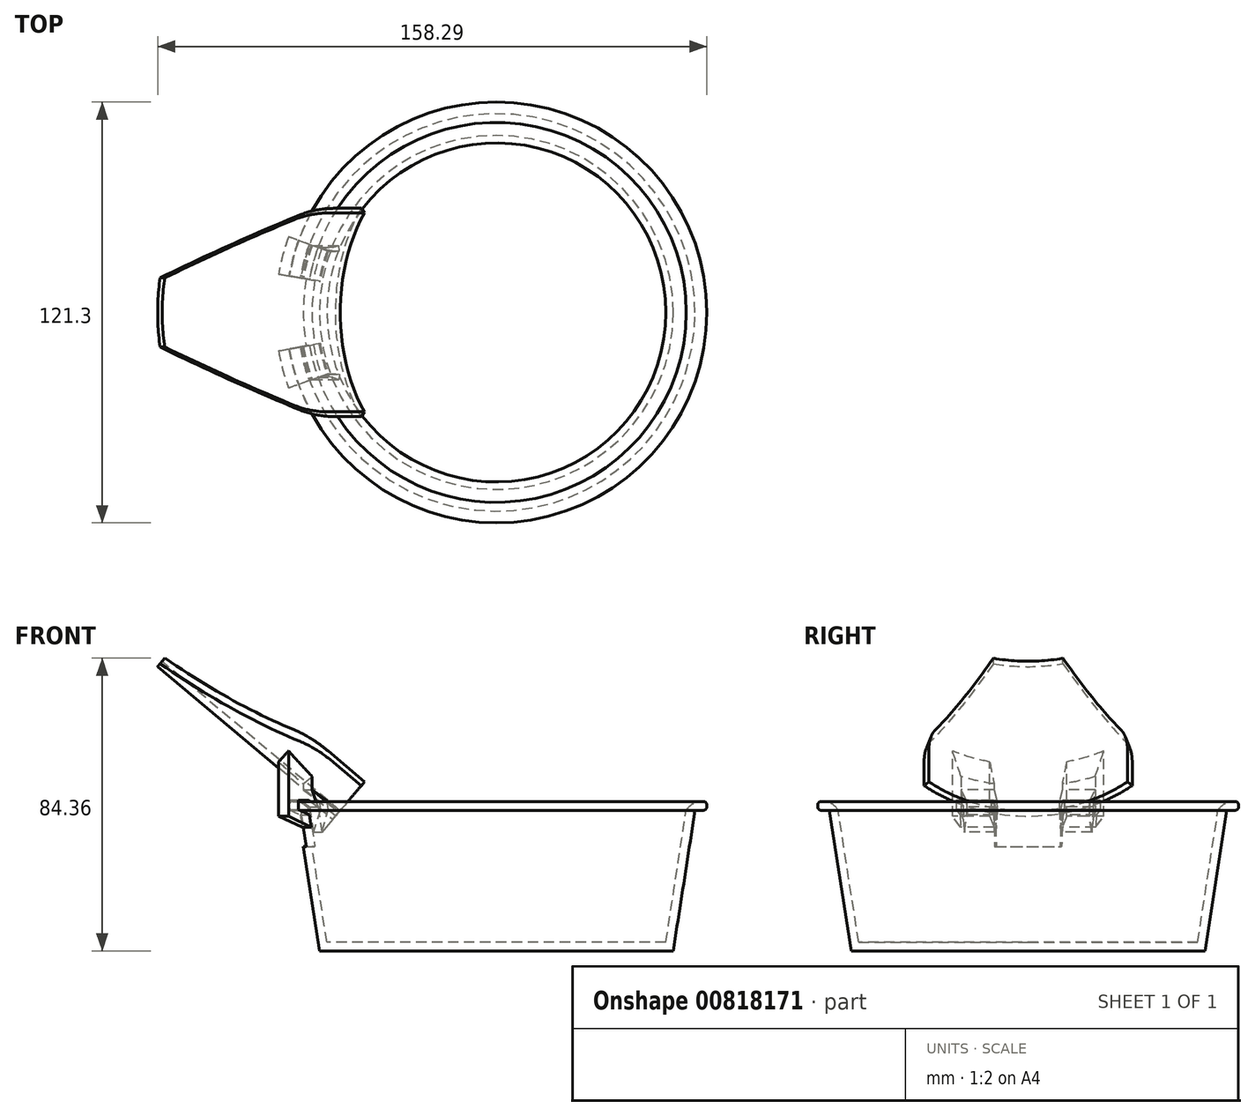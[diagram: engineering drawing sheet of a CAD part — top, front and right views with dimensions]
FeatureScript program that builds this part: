
annotation { "Feature Type Name" : "Feature", "Feature Type Description" : "" }
export const myFeature = defineFeature(function(context is Context, id is Id, definition is map)
    precondition{}
    {
        {
            var Q0;
            Q0=qCreatedBy(makeId("Front.planeOp"),FACE);
            var sketch = newSketch(context, id + "F0", { "sketchPlane" : qUnion([Q0])});
            skLineSegment(sketch, "E0", {"start": v(0, 0) * mm, "end": v(0, 46.12) * mm, "construction": true});
            skSolve(sketch);
        }
        {
            var Q0;
            Q0=qCreatedBy(makeId("Top.planeOp"),FACE);
            var sketch = newSketch(context, id + "F1", { "sketchPlane" : qUnion([Q0])});
            skCircle(sketch, "E1", {"center": v(0, 0) * mm, "radius": 51 * mm});
            skSolve(sketch);
        }
        {
            var Q0;
            Q0=qCreatedBy(makeId("Top.planeOp"),FACE);
            cPlane(context, id + "F2", {"entities" : qUnion([Q0]), "cplaneType" : CPlaneType.OFFSET, "offset" : 40.5 * mm, "width" : 150 * mm, "height" : 150 * mm});
        }
        {
            var Q0;
            Q0=qCreatedBy(id+"F2.planeOp",FACE);
            var sketch = newSketch(context, id + "F3", { "sketchPlane" : qUnion([Q0])});
            skCircle(sketch, "E2", {"center": v(0, 0) * mm, "radius": 57.27 * mm});
            skSolve(sketch);
        }
        {
            var Q0;
            Q0=makeQuery(id+"F1.imprint","IMPRINT",FACE,{"disambiguationData":[TD([[makeQuery(id+"F1.imprint","IMPRINT",EDGE,{"derivedFrom":sQuery(id+"F1.wireOp",EDGE,"E1")}),1.0]])]});
            var Q1;
            Q1=makeQuery(id+"F3.imprint","IMPRINT",FACE,{"disambiguationData":[TD([[makeQuery(id+"F3.imprint","IMPRINT",EDGE,{"derivedFrom":sQuery(id+"F3.wireOp",EDGE,"E2")}),1.0]])]});
            loft(context, id + "F4", {"sheetProfilesArray" : [{ "sheetProfileEntities" : qUnion([Q0]) }, { "sheetProfileEntities" : qUnion([Q1]) }]});
        }
        {
            var Q0;
            Q0=makeQuery(id+"F4.opLoft","CAP_FACE",FACE,{"disambiguationData":[OSD([makeQuery(id+"F3.imprint","IMPRINT",FACE,{"disambiguationData":[TD([[makeQuery(id+"F3.imprint","IMPRINT",EDGE,{"derivedFrom":sQuery(id+"F3.wireOp",EDGE,"E2")}),1.0]])]})])],"isStart":true});
            var sketch = newSketch(context, id + "F5", { "sketchPlane" : qUnion([Q0])});
            skCircle(sketch, "E3", {"center": v(0, 0) * mm, "radius": 60.65 * mm});
            skSolve(sketch);
        }
        {
            var Q0;
            Q0=makeQuery(id+"F4.opLoft","CAP_FACE",FACE,{"disambiguationData":[OSD([makeQuery(id+"F3.imprint","IMPRINT",FACE,{"disambiguationData":[TD([[makeQuery(id+"F3.imprint","IMPRINT",EDGE,{"derivedFrom":sQuery(id+"F3.wireOp",EDGE,"E2")}),1.0]])]})])],"isStart":true});
            shell(context, id + "F6", {"entities" : qUnion([Q0]), "thickness" : 2.5 * mm});
        }
        {
            var Q0;
            Q0=makeQuery(id+"F5.imprint","IMPRINT",FACE,{"disambiguationData":[TD([[makeQuery(id+"F5.imprint","IMPRINT",EDGE,{"derivedFrom":sQuery(id+"F5.wireOp",EDGE,"E3")}),1.0]])]});
            var Q1;
            Q1=makeQuery(id+"F4.opLoft","CAP_FACE",FACE,{"disambiguationData":[OSD([makeQuery(id+"F3.imprint","IMPRINT",FACE,{"disambiguationData":[TD([[makeQuery(id+"F3.imprint","IMPRINT",EDGE,{"derivedFrom":sQuery(id+"F3.wireOp",EDGE,"E2")}),1.0]])]})])],"isStart":true});
            extrude(context, id + "F7", {"entities" : qUnion([Q0, Q1]), "operationType" : NewBodyOperationType.ADD, "depth" : 2.55 * mm, "offsetDistance" : 25 * mm});
        }
        {
            var Q0;
            Q0=makeQuery(id+"F7.opExtrude","CAP_EDGE",EDGE,{"disambiguationData":[OSD([sQuery(id+"F5.wireOp",EDGE,"E3")])],"isStart":false});
            var Q1;
            Q1=makeQuery(id+"F7.opExtrude","CAP_EDGE",EDGE,{"disambiguationData":[OSD([sQuery(id+"F5.wireOp",EDGE,"E3")])],"isStart":true});
            fillet(context, id + "F8", {"entities" : qUnion([Q0, Q1]), "radius" : 1 * mm, "tangentPropagation" : true, "allowEdgeOverflow" : false});
        }
        {
            var Q0;
            {var subQ0=sQuery(id+"F3.wireOp",EDGE,"E2");Q0=makeQuery(id+"F7.opExtrude","CAP_EDGE",EDGE,{"disambiguationData":[OSD([subQ0]),TDD([makeQuery(id+"F6.opShell","OFFSET_EDGE",EDGE,{"disambiguationData":[OSD([subQ0])]})])],"isStart":false});}
            fillet(context, id + "F9", {"entities" : qUnion([Q0]), "radius" : 5 * mm, "tangentPropagation" : true, "allowEdgeOverflow" : false});
        }
        {
            var Q0;
            Q0=qCreatedBy(makeId("Front.planeOp"),FACE);
            var sketch = newSketch(context, id + "F10", { "sketchPlane" : qUnion([Q0])});
            skLineSegment(sketch, "E4", {"start": v(-57.38, 39.2) * mm, "end": v(-56.83, 35.67) * mm});
            skLineSegment(sketch, "E5", {"start": v(-56.83, 35.67) * mm, "end": v(-63.75, 38.75) * mm});
            skLineSegment(sketch, "E6", {"start": v(-63.75, 38.75) * mm, "end": v(-63.75, 46.4) * mm});
            skLineSegment(sketch, "E7", {"start": v(-63.75, 46.4) * mm, "end": v(-60.75, 46.4) * mm});
            skLineSegment(sketch, "E8", {"start": v(-60.75, 46.4) * mm, "end": v(-60.75, 40.7) * mm});
            skLineSegment(sketch, "E9", {"start": v(-60.75, 40.7) * mm, "end": v(-57.38, 39.2) * mm});
            skLineSegment(sketch, "E10", {"start": v(-60.75, 43.4) * mm, "end": v(-57.45, 43.4) * mm});
            skLineSegment(sketch, "E11", {"start": v(-57.45, 43.4) * mm, "end": v(-54.7, 41.5) * mm});
            skLineSegment(sketch, "E12", {"start": v(-54.7, 41.5) * mm, "end": v(-53.57, 34.22) * mm});
            skLineSegment(sketch, "E13", {"start": v(-53.57, 34.22) * mm, "end": v(-51.55, 40.76) * mm});
            skLineSegment(sketch, "E14", {"start": v(-51.55, 40.76) * mm, "end": v(-51.93, 43.23) * mm});
            skLineSegment(sketch, "E15", {"start": v(-51.93, 43.23) * mm, "end": v(-56.5, 46.4) * mm});
            skLineSegment(sketch, "E16", {"start": v(-56.5, 46.4) * mm, "end": v(-60.75, 46.4) * mm});
            skLineSegment(sketch, "E17", {"start": v(-48.86, 2.5) * mm, "end": v(-54.75, 40.5) * mm, "construction": true});
            skSolve(sketch);
        }
        {
            var Q0;
            Q0=qSketchRegion(id+"F10",true);
            var Q1;
            Q1=sQuery(id+"F0.wireOp",EDGE,"E0");
            revolve(context, id + "F11", {"surfaceOperationType" : NewSurfaceOperationType.NEW, "entities" : qUnion([Q0]), "axis" : qUnion([Q1]), "revolveType" : RevolveType.SYMMETRIC, "oppositeDirection" : true, "angle" : 40 * degree});
        }
        {
            var Q0;
            Q0=qCreatedBy(makeId("Front.planeOp"),FACE);
            var sketch = newSketch(context, id + "F12", { "sketchPlane" : qUnion([Q0])});
            skLineSegment(sketch, "E18.bottom", {"start": v(-70, 50) * mm, "end": v(-40, 50) * mm});
            skLineSegment(sketch, "E18.top", {"start": v(-70, 30) * mm, "end": v(-40, 30) * mm});
            skLineSegment(sketch, "E18.left", {"start": v(-70, 50) * mm, "end": v(-70, 30) * mm});
            skLineSegment(sketch, "E18.right", {"start": v(-40, 50) * mm, "end": v(-40, 30) * mm});
            skSolve(sketch);
        }
        {
            var Q0;
            Q0=qSketchRegion(id+"F12",true);
            var Q1;
            Q1=sQuery(id+"F0.wireOp",EDGE,"E0");
            revolve(context, id + "F13", {"operationType" : NewBodyOperationType.REMOVE, "surfaceOperationType" : NewSurfaceOperationType.NEW, "entities" : qUnion([Q0]), "axis" : qUnion([Q1]), "revolveType" : RevolveType.SYMMETRIC, "oppositeDirection" : true, "angle" : 20 * degree});
        }
        {
            var Q0;
            {var subQ0=sQuery(id+"F10.wireOp",EDGE,"E16");var subQ2=sQuery(id+"F10.wireOp",EDGE,"E7");Q0=makeQuery(id+"F13.boolean.opBoolean","SPLIT",FACE,{"disambiguationData":[TD([makeQuery(id+"F13.opRevolve","CAP_FACE",FACE,{"disambiguationData":[OSD([sQuery(id+"F12.wireOp",EDGE,"E18.bottom"),sQuery(id+"F12.wireOp",EDGE,"E18.top"),sQuery(id+"F12.wireOp",EDGE,"E18.left"),sQuery(id+"F12.wireOp",EDGE,"E18.right")])],"isStart":false})])],"derivedFrom":makeQuery(id+"F11.opRevolve","SWEPT_FACE",FACE,{"disambiguationData":[OSD([subQ2,subQ0])]})});}
            var sketch = newSketch(context, id + "F14", { "sketchPlane" : qUnion([Q0])});
            skLineSegment(sketch, "E19", {"start": v(-55.65, 9.81) * mm, "end": v(-55.65, -9.81) * mm, "construction": true});
            skSolve(sketch);
        }
        {
            var Q0;
            Q0=sQuery(id+"F14.wireOp",EDGE,"E19");
            cPlane(context, id + "F15", {"entities" : qUnion([Q0]), "cplaneType" : CPlaneType.LINE_ANGLE, "offset" : 25 * mm, "angle" : 50 * degree, "width" : 150 * mm, "height" : 150 * mm});
        }
        {
            var Q0;
            Q0=qCreatedBy(id+"F15.planeOp",FACE);
            var sketch = newSketch(context, id + "F16", { "sketchPlane" : qUnion([Q0])});
            skCircle(sketch, "E20", {"center": v(0, 45) * mm, "radius": 45 * mm});
            skCircle(sketch, "E21", {"center": v(0, 45) * mm, "radius": 43 * mm});
            skLineSegment(sketch, "E22", {"start": v(0, 45) * mm, "end": v(-30, 11.46) * mm});
            skLineSegment(sketch, "E23", {"start": v(0, 45) * mm, "end": v(30, 11.46) * mm});
            skSolve(sketch);
        }
        {
            var Q0;
            {var subQ0=sQuery(id+"F16.wireOp",EDGE,"E22");var subQ1=sQuery(id+"F16.wireOp",EDGE,"E20");var subQ2=makeQuery(id+"F16.imprint","INTERSECT",VERTEX,{"derivedFrom":[subQ1,subQ0]});Q0=makeQuery(id+"F16.imprint","IMPRINT",FACE,{"disambiguationData":[TD([[makeQuery(id+"F16.imprint","IMPRINT",EDGE,{"disambiguationData":[TD([[subQ2,-1.0]])],"derivedFrom":subQ1}),1.0]])]});}
            extrude(context, id + "F17", {"entities" : qUnion([Q0]), "depth" : 12 * mm, "offsetDistance" : 25 * mm, "hasSecondDirection" : true, "secondDirectionOppositeDirection" : true, "secondDirectionDepth" : 55 * mm});
        }
        {
            var Q0;
            {var subQ0=sQuery(id+"F10.wireOp",EDGE,"E16");var subQ2=sQuery(id+"F10.wireOp",EDGE,"E7");Q0=makeQuery(id+"F13.boolean.opBoolean","SPLIT",FACE,{"disambiguationData":[TD([makeQuery(id+"F13.opRevolve","CAP_FACE",FACE,{"disambiguationData":[OSD([sQuery(id+"F12.wireOp",EDGE,"E18.bottom"),sQuery(id+"F12.wireOp",EDGE,"E18.top"),sQuery(id+"F12.wireOp",EDGE,"E18.left"),sQuery(id+"F12.wireOp",EDGE,"E18.right")])],"isStart":true})])],"derivedFrom":makeQuery(id+"F11.opRevolve","SWEPT_FACE",FACE,{"disambiguationData":[OSD([subQ2,subQ0])]})});}
            var Q1;
            {var subQ0=sQuery(id+"F10.wireOp",EDGE,"E16");var subQ1=sQuery(id+"F10.wireOp",EDGE,"E7");Q1=makeQuery(id+"F14.imprint","IMPRINT",FACE,{"disambiguationData":[TD([[makeQuery(id+"F14.imprint","IMPRINT",EDGE,{"derivedFrom":makeQuery(id+"F11.opRevolve","CAP_EDGE",EDGE,{"disambiguationData":[OSD([subQ1,subQ0])],"isStart":false})}),-1.0]])]});}
            var Q2;
            Q2=makeQuery(id+"F17.opExtrude","SWEPT_BODY",BODY,{"disambiguationData":[OSD([sQuery(id+"F16.wireOp",EDGE,"E20"),sQuery(id+"F16.wireOp",EDGE,"E21"),sQuery(id+"F16.wireOp",EDGE,"E22"),sQuery(id+"F16.wireOp",EDGE,"E23")])]});
            extrude(context, id + "F18", {"entities" : qUnion([Q0, Q1]), "operationType" : NewBodyOperationType.ADD, "endBound" : BoundingType.UP_TO_BODY, "depth" : 25 * mm, "endBoundEntityBody" : qUnion([Q2]), "offsetDistance" : 25 * mm});
        }
        {
            var Q0;
            Q0=makeQuery(id+"F17.opExtrude","CAP_VERTEX",VERTEX,{"disambiguationData":[OSD([sQuery(id+"F16.wireOp",EDGE,"E21"),sQuery(id+"F16.wireOp",EDGE,"E23")])],"isStart":true});
            var Q1;
            Q1=makeQuery(id+"F17.opExtrude","CAP_VERTEX",VERTEX,{"disambiguationData":[OSD([sQuery(id+"F16.wireOp",EDGE,"E21"),sQuery(id+"F16.wireOp",EDGE,"E22")])],"isStart":true});
            var Q2;
            Q2=makeQuery(id+"F17.opExtrude","CAP_VERTEX",VERTEX,{"disambiguationData":[OSD([sQuery(id+"F16.wireOp",EDGE,"E21"),sQuery(id+"F16.wireOp",EDGE,"E22")])],"isStart":false});
            cPlane(context, id + "F19", {"entities" : qUnion([Q0, Q1, Q2]), "cplaneType" : CPlaneType.THREE_POINT, "offset" : 25 * mm, "width" : 150 * mm, "height" : 150 * mm});
        }
        {
            var Q0;
            Q0=qCreatedBy(id+"F19.planeOp",FACE);
            var sketch = newSketch(context, id + "F20", { "sketchPlane" : qUnion([Q0])});
            skLineSegment(sketch, "E24", {"start": v(-127.46, 0) * mm, "end": v(-56.5, 0) * mm, "construction": true});
            skLineSegment(sketch, "E25", {"start": v(-127.46, 10) * mm, "end": v(-77.46, 30) * mm});
            skLineSegment(sketch, "E26", {"start": v(-77.46, 30) * mm, "end": v(-127.46, 30) * mm});
            skLineSegment(sketch, "E27", {"start": v(-127.46, 30) * mm, "end": v(-127.46, 10) * mm});
            skLineSegment(sketch, "E28.MirrorCS", {"start": v(-127.46, -10) * mm, "end": v(-77.46, -30) * mm});
            skLineSegment(sketch, "E29.MirrorCS", {"start": v(-127.46, -30) * mm, "end": v(-127.46, -10) * mm});
            skLineSegment(sketch, "E30.MirrorCS", {"start": v(-77.46, -30) * mm, "end": v(-127.46, -30) * mm});
            skSolve(sketch);
        }
        {
            var Q0;
            Q0=makeQuery(id+"F20.imprint","IMPRINT",FACE,{"disambiguationData":[TD([[makeQuery(id+"F20.imprint","IMPRINT",EDGE,{"derivedFrom":sQuery(id+"F20.wireOp",EDGE,"E25")}),1.0]])]});
            var Q1;
            Q1=makeQuery(id+"F20.imprint","IMPRINT",FACE,{"disambiguationData":[TD([[makeQuery(id+"F20.imprint","IMPRINT",EDGE,{"derivedFrom":sQuery(id+"F20.wireOp",EDGE,"E28.MirrorCS")}),-1.0]])]});
            extrude(context, id + "F21", {"entities" : qUnion([Q0, Q1]), "operationType" : NewBodyOperationType.REMOVE, "endBound" : BoundingType.THROUGH_ALL, "depth" : 25 * mm, "offsetDistance" : 25 * mm});
        }
        {
            var Q0;
            Q0=makeQuery(id+"F21.boolean.opBoolean","COPY",EDGE,{"derivedFrom":makeQuery(id+"F21.opExtrude","SWEPT_EDGE",EDGE,{"disambiguationData":[OSD([sQuery(id+"F20.wireOp",EDGE,"E25"),sQuery(id+"F20.wireOp",EDGE,"E27")])]})});
            var Q1;
            Q1=makeQuery(id+"F21.boolean.opBoolean","COPY",EDGE,{"derivedFrom":makeQuery(id+"F21.opExtrude","SWEPT_EDGE",EDGE,{"disambiguationData":[OSD([sQuery(id+"F20.wireOp",EDGE,"E28.MirrorCS"),sQuery(id+"F20.wireOp",EDGE,"E29.MirrorCS")])]})});
            var Q2;
            Q2=makeQuery(id+"F21.boolean.opBoolean","INTERSECT",EDGE,{"derivedFrom":[makeQuery(id+"F17.opExtrude","SWEPT_FACE",FACE,{"disambiguationData":[OSD([sQuery(id+"F16.wireOp",EDGE,"E22")])]}),makeQuery(id+"F21.opExtrude","SWEPT_FACE",FACE,{"disambiguationData":[OSD([sQuery(id+"F20.wireOp",EDGE,"E25")])]})]});
            var Q3;
            Q3=makeQuery(id+"F21.boolean.opBoolean","INTERSECT",EDGE,{"derivedFrom":[makeQuery(id+"F17.opExtrude","SWEPT_FACE",FACE,{"disambiguationData":[OSD([sQuery(id+"F16.wireOp",EDGE,"E23")])]}),makeQuery(id+"F21.opExtrude","SWEPT_FACE",FACE,{"disambiguationData":[OSD([sQuery(id+"F20.wireOp",EDGE,"E28.MirrorCS")])]})]});
            fillet(context, id + "F22", {"entities" : qUnion([Q0, Q1, Q2, Q3]), "radius" : 8 * mm, "tangentPropagation" : true, "allowEdgeOverflow" : false});
        }
        {
            var Q0;
            Q0=makeQuery(id+"F17.opExtrude","CAP_FACE",FACE,{"disambiguationData":[OSD([sQuery(id+"F16.wireOp",EDGE,"E20"),sQuery(id+"F16.wireOp",EDGE,"E21"),sQuery(id+"F16.wireOp",EDGE,"E22"),sQuery(id+"F16.wireOp",EDGE,"E23")])],"isStart":false});
            var sketch = newSketch(context, id + "F23", { "sketchPlane" : qUnion([Q0])});
            skArc(sketch, "E31.0", {"start": v(-30, 11.46) * mm, "mid": v(0, 0) * mm, "end": v(30, 11.46) * mm});
            skLineSegment(sketch, "E31.1", {"start": v(-19.33, 4.36) * mm, "end": v(-19.33, 1.41) * mm});
            skLineSegment(sketch, "E31.2", {"start": v(-17.76, 1.75) * mm, "end": v(-19.33, 1.41) * mm});
            skLineSegment(sketch, "E31.3", {"start": v(-17.63, 0.1) * mm, "end": v(-17.76, 1.75) * mm});
            skLineSegment(sketch, "E31.4", {"start": v(-18.32, -6.14) * mm, "end": v(-17.63, 0.1) * mm});
            skEllipticalArc(sketch, "E31.5", {});
            skLineSegment(sketch, "E31.6", {"start": v(-8.95, -1.4) * mm, "end": v(-9.3, -7.7) * mm});
            skLineSegment(sketch, "E31.7", {"start": v(-9.02, 0.25) * mm, "end": v(-8.95, -1.4) * mm});
            skLineSegment(sketch, "E31.8", {"start": v(-9.81, -0.23) * mm, "end": v(-9.02, 0.25) * mm});
            skLineSegment(sketch, "E31.9", {"start": v(-9.81, 1.08) * mm, "end": v(-9.81, -0.23) * mm});
            skLineSegment(sketch, "E31.10", {"start": v(8.95, -1.4) * mm, "end": v(9.3, -7.7) * mm});
            skLineSegment(sketch, "E31.11", {"start": v(9.02, 0.25) * mm, "end": v(8.95, -1.4) * mm});
            skLineSegment(sketch, "E31.12", {"start": v(9.81, -0.23) * mm, "end": v(9.02, 0.25) * mm});
            skLineSegment(sketch, "E31.13", {"start": v(9.81, 1.08) * mm, "end": v(9.81, -0.23) * mm});
            skEllipticalArc(sketch, "E31.14", {});
            skLineSegment(sketch, "E31.15", {"start": v(18.32, -6.14) * mm, "end": v(17.63, 0.1) * mm});
            skLineSegment(sketch, "E31.16", {"start": v(17.63, 0.1) * mm, "end": v(17.76, 1.75) * mm});
            skLineSegment(sketch, "E31.17", {"start": v(17.76, 1.75) * mm, "end": v(19.33, 1.41) * mm});
            skLineSegment(sketch, "E31.18", {"start": v(19.33, 4.36) * mm, "end": v(19.33, 1.41) * mm});
            skLineSegment(sketch, "E32.0", {"start": v(-18.7, -1.25) * mm, "end": v(-18.32, -6.14) * mm});
            skLineSegment(sketch, "E32.1", {"start": v(18.7, -1.25) * mm, "end": v(18.32, -6.14) * mm});
            skLineSegment(sketch, "E33", {"start": v(-18.7, -1.25) * mm, "end": v(-19.33, 1.41) * mm});
            skLineSegment(sketch, "E34", {"start": v(18.7, -1.25) * mm, "end": v(19.33, 1.41) * mm});
            const initialGuessF23  = {"E31.5": [0, 0.03162733839321066, 1, 0, 0.053674650700035235, 0.022683887578388108, 4.363323129985824, 4.537856055185257], "E31.14": [0, 0.03162733839321066, 1, 0, 0.053674650700035235, 0.022683887578388108, 4.886921905584122, 5.061454830783555]};
            skSetInitialGuess(sketch, initialGuessF23);
            skSolve(sketch);
        }
        {
            var Q0;
            Q0=qSketchRegion(id+"F23",true);
            var Q1;
            Q1=makeQuery(id+"F13.boolean.opBoolean","SPLIT",BODY,{"disambiguationData":[OD(0.0)],"derivedFrom":makeQuery(id+"F11.opRevolve","SWEPT_BODY",BODY,{"disambiguationData":[OSD([sQuery(id+"F10.wireOp",EDGE,"E4"),sQuery(id+"F10.wireOp",EDGE,"E5"),sQuery(id+"F10.wireOp",EDGE,"E6"),sQuery(id+"F10.wireOp",EDGE,"E7"),sQuery(id+"F10.wireOp",EDGE,"E8"),sQuery(id+"F10.wireOp",EDGE,"E9"),sQuery(id+"F10.wireOp",EDGE,"E10"),sQuery(id+"F10.wireOp",EDGE,"E11"),sQuery(id+"F10.wireOp",EDGE,"E12"),sQuery(id+"F10.wireOp",EDGE,"E13"),sQuery(id+"F10.wireOp",EDGE,"E14"),sQuery(id+"F10.wireOp",EDGE,"E15"),sQuery(id+"F10.wireOp",EDGE,"E16")])]})});
            extrude(context, id + "F24", {"entities" : qUnion([Q0]), "operationType" : NewBodyOperationType.ADD, "endBound" : BoundingType.UP_TO_BODY, "oppositeDirection" : true, "depth" : 25 * mm, "endBoundEntityBody" : qUnion([Q1]), "offsetDistance" : 25 * mm});
        }
    });
